# Revit family: Gas-Detector-Controller-DVP-120-Aerionics
name_source: partatom
category: Mechanical Equipment
units: mm (PartAtom-declared; Revit-internal decimal feet)

## family parameters
Always vertical = Yes
Classification Number = 23.65.00.00
Cut with Voids When Loaded = No
Host = Wall
Maintain Annotation Orientation = No
Part Type = Normal
Room Calculation Point = No
Round Connector Dimension = Use Diameter
Shared = No

## types (4) — shared parameters
Categories = Control Panels, HVAC/R, Electrical
Manufacturer = MACURCO
Tags = Arenas, Commercial Applications, Loading Docks, Parking Garages, Warehouses
Type Comments = Do not paint
URL = https://www.macurco.com
zero-valued in all types: Default Elevation

## per-type parameters (varying)
| type | Comments | Model Name |
| DVP-120 | The DVP-120 exhaust fan controller, in conjunction with Macurco™ gas transducers, provides automatic controls to help maintain an acceptable environment in parking garages or other facilities – ETL Listed, LADBS Approved | DVP-120-Analog |
| DVP-120B | The DVP-120B is a BACnet Control Panel providing automatic control to help maintain an acceptable environment in parking garages or other facilities. The DVP-120B can control up to 99 addressable gas detectors – ETL Listed | DVP-120B-Digital w/ BACnet output |
| DVP-120C | The DVP-120C is a BACnet Control Panel providing automatic control to help maintain an acceptable environment in parking garages or other facilities. The DVP-120C can control up to 99 addressable Macurco CM-6 and TX-6-ND detectors in conjunction with the Macurco MRS-485 adapter. – ETL Listed to UL 2017 | DVP-120C-Designed to comply with Title 24 |
| DVP-120M | The DVP-120M exhaust fan controller provides automatic control to help maintain an acceptable environment in parking garages or other facilities. Using the Macurco MRS-485 Modbus adapter and 6-Series detectors, the DVP-120M can control up to 87 addressable gas detectors – ETL Listed | DVP-120M-Digital |

## geometry (parser evidence)
native form markers: Sweep x3
no freeform markers — native parametric forms only
